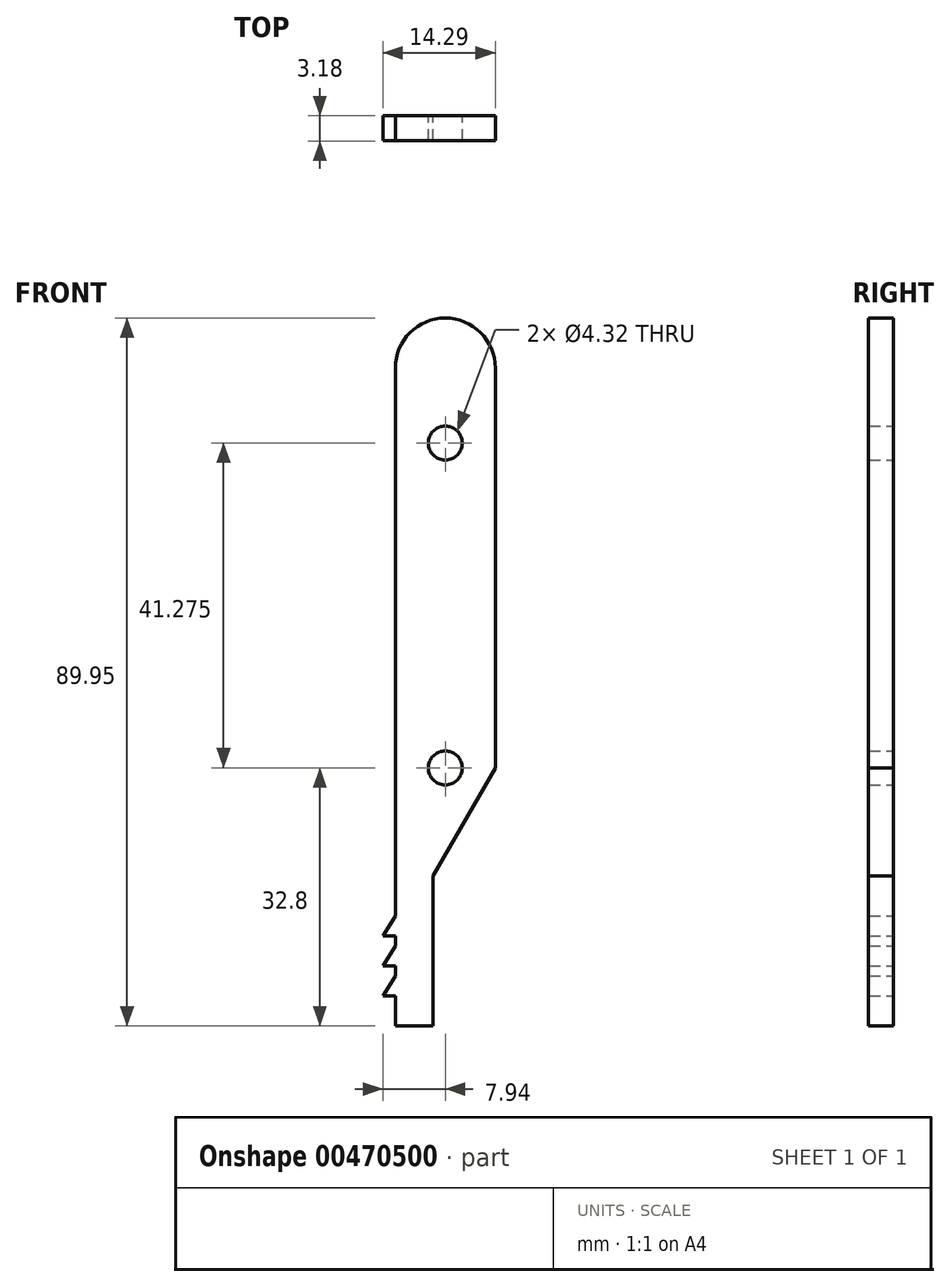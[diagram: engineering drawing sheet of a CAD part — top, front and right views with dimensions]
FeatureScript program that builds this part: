
annotation { "Feature Type Name" : "Feature", "Feature Type Description" : "" }
export const myFeature = defineFeature(function(context is Context, id is Id, definition is map)
    precondition{}
    {
        {
            var Q0;
            Q0=qCreatedBy(makeId("Front.planeOp"),FACE);
            var sketch = newSketch(context, id + "F0", { "sketchPlane" : qUnion([Q0])});
            skLineSegment(sketch, "E0.bottom", {"start": v(0, 0) * mm, "end": v(12.7, 0) * mm});
            skLineSegment(sketch, "E0.top", {"start": v(0, 50.8) * mm, "end": v(12.7, 50.8) * mm});
            skLineSegment(sketch, "E0.left", {"start": v(0, 0) * mm, "end": v(0, 50.8) * mm});
            skLineSegment(sketch, "E0.right", {"start": v(12.7, 0) * mm, "end": v(12.7, 50.8) * mm});
            skArc(sketch, "E1", {"start": v(12.7, 50.8) * mm, "mid": v(6.35, 57.15) * mm, "end": v(0, 50.8) * mm});
            skLineSegment(sketch, "E2", {"start": v(0, 0) * mm, "end": v(0, -32.8) * mm});
            skLineSegment(sketch, "E3", {"start": v(4.76, -32.8) * mm, "end": v(0, -32.8) * mm});
            skLineSegment(sketch, "E4", {"start": v(4.76, -32.8) * mm, "end": v(4.76, -13.75) * mm});
            skLineSegment(sketch, "E5", {"start": v(12.7, 0) * mm, "end": v(4.76, -13.75) * mm});
            skLineSegment(sketch, "E6", {"start": v(0, -28.99) * mm, "end": v(-1.59, -28.99) * mm});
            skLineSegment(sketch, "E7", {"start": v(0, -26.45) * mm, "end": v(-1.59, -28.99) * mm});
            skLineSegment(sketch, "E8", {"start": v(0, -25.18) * mm, "end": v(-1.59, -25.18) * mm});
            skLineSegment(sketch, "E9", {"start": v(0, -22.64) * mm, "end": v(-1.59, -25.18) * mm});
            skLineSegment(sketch, "E10", {"start": v(0, -21.37) * mm, "end": v(-1.59, -21.37) * mm});
            skLineSegment(sketch, "E11", {"start": v(-1.59, -21.37) * mm, "end": v(0, -18.83) * mm});
            skCircle(sketch, "E12", {"center": v(6.35, 0) * mm, "radius": 2.16 * mm});
            skCircle(sketch, "E13", {"center": v(6.35, 41.28) * mm, "radius": 2.16 * mm});
            skSolve(sketch);
        }
        {
            var Q0;
            Q0 = qSketchRegion(id + "F0", true);
            extrude(context, id + "F1", {"entities" : qUnion([Q0]), "depth" : 3.17 * mm});
        }
    });
